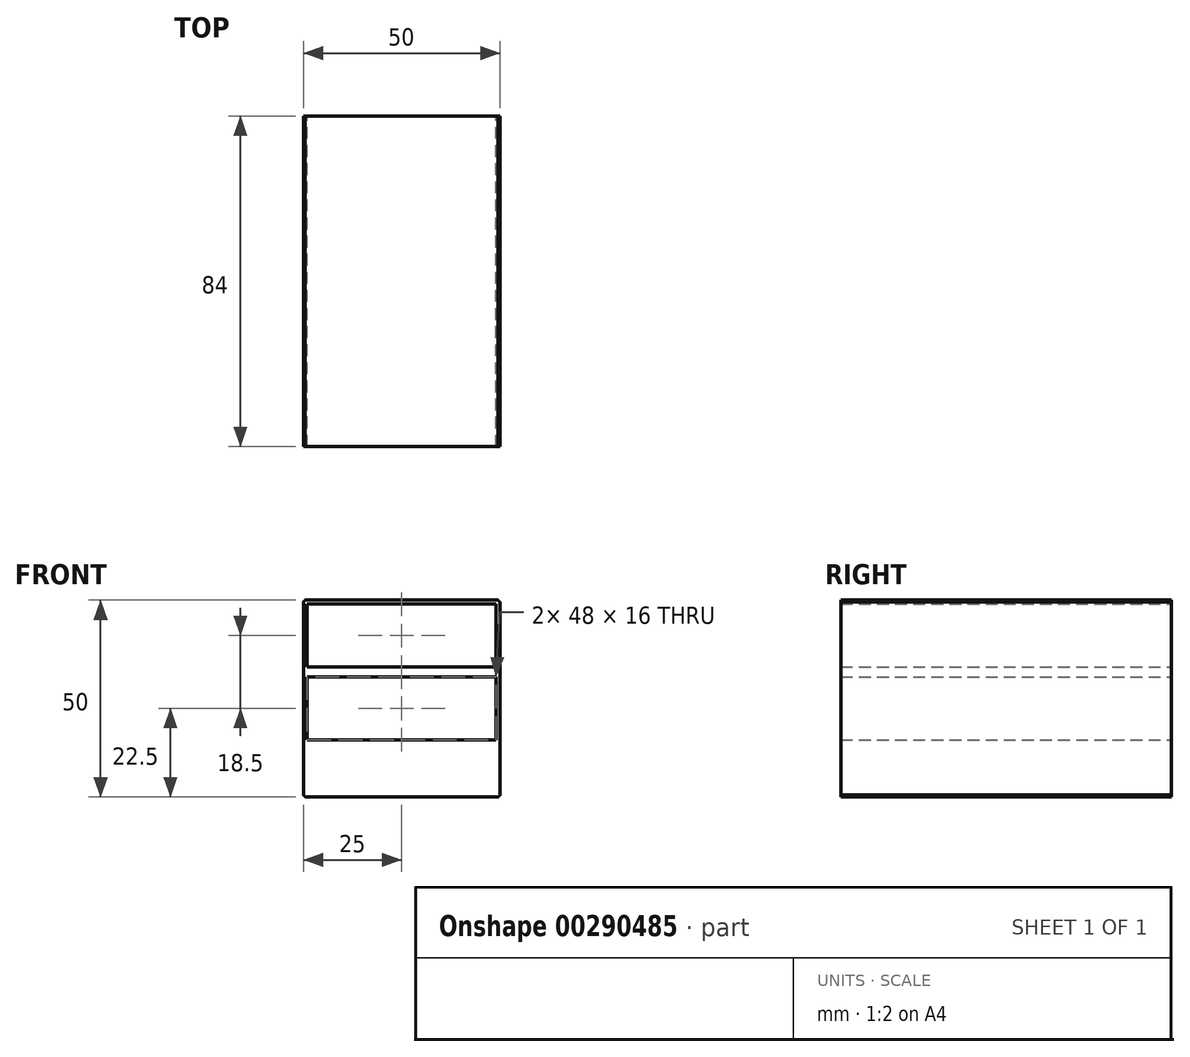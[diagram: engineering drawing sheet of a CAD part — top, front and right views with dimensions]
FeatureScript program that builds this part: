
annotation { "Feature Type Name" : "Feature", "Feature Type Description" : "" }
export const myFeature = defineFeature(function(context is Context, id is Id, definition is map)
    precondition{}
    {
        {
            var Q0;
            Q0=qCreatedBy(makeId("Front.planeOp"),FACE);
            var sketch = newSketch(context, id + "F0", { "sketchPlane" : qUnion([Q0])});
            skCircle(sketch, "E0", {"center": v(0, 0) * mm, "radius": 35 * mm});
            skLineSegment(sketch, "E1.bottom", {"start": v(24, 8) * mm, "end": v(-24, 8) * mm});
            skLineSegment(sketch, "E1.top", {"start": v(24, 24) * mm, "end": v(-24, 24) * mm});
            skLineSegment(sketch, "E1.left", {"start": v(24, 8) * mm, "end": v(24, 24) * mm});
            skLineSegment(sketch, "E1.right", {"start": v(-24, 8) * mm, "end": v(-24, 24) * mm});
            skPoint(sketch, "E1.middle", {"position": v(0, 16) * mm});
            skLineSegment(sketch, "E2.bottom", {"start": v(25, 25) * mm, "end": v(-25, 25) * mm});
            skLineSegment(sketch, "E2.top", {"start": v(25, -25) * mm, "end": v(-25, -25) * mm});
            skLineSegment(sketch, "E2.left", {"start": v(25, 25) * mm, "end": v(25, -25) * mm});
            skLineSegment(sketch, "E2.right", {"start": v(-25, 25) * mm, "end": v(-25, -25) * mm});
            skLineSegment(sketch, "E3.0.1.0", {"start": v(24, -10.5) * mm, "end": v(-24, -10.5) * mm});
            skLineSegment(sketch, "E3.0.1.1", {"start": v(-24, -10.5) * mm, "end": v(-24, 5.5) * mm});
            skLineSegment(sketch, "E3.0.1.2", {"start": v(24, 5.5) * mm, "end": v(-24, 5.5) * mm});
            skLineSegment(sketch, "E3.0.1.3", {"start": v(24, -10.5) * mm, "end": v(24, 5.5) * mm});
            skLineSegment(sketch, "E3.direction1", {"start": v(-24, 8) * mm, "end": v(1, 8) * mm, "construction": true});
            skLineSegment(sketch, "E3.direction2", {"start": v(-24, 8) * mm, "end": v(-24, -10.5) * mm, "construction": true});
            skPoint(sketch, "E4", {"position": v(25, -24.5) * mm});
            skSolve(sketch);
        }
        {
            var Q0;
            Q0=makeQuery(id+"F0.imprint","IMPRINT",FACE,{"disambiguationData":[TD([[makeQuery(id+"F0.imprint","IMPRINT",EDGE,{"derivedFrom":sQuery(id+"F0.wireOp",EDGE,"E0")}),1.0]])]});
            extrude(context, id + "F1", {"entities" : qUnion([Q0]), "depth" : 84 * mm});
        }
    });
